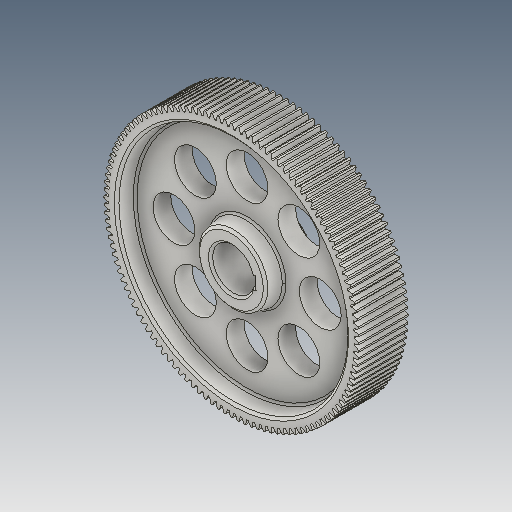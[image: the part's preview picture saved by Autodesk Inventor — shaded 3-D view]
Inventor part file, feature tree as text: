
AUTODESK INVENTOR PART (.ipt)
format: ipt  version: 2025 (Build 290162000, 162)  size: 833,024 bytes
history: native  units: mm (DEFAULTED — no unit token found)
features: other x5, sketch x5, extrude x4, plane x3, mirror x1, fillet x1, chamfer x1
ambient origin geometry x8: Origin, YZ Plane, XZ Plane, XY Plane, X Axis, Y Axis, Z Axis, Center Point
bodies: Solid1 (feature_tree)
feature tree (20):
  other  "{BB8FE430-83BF-418D-8DF9-9B323D3DB9B9}"
  extrude  "Extrusion1"  Depth=47.0mm TaperAngle=0.0deg
  plane  "Work Plane2"
  plane  "Work Plane8"
  plane  "Work Plane9"
  other  "正齿轮"
  extrude  "拉伸2"  Depth=10.0mm TaperAngle=0.0deg
  extrude  "拉伸3"  Depth=0.261799mm TaperAngle=0.0deg
  mirror  "镜像1"
  extrude  "拉伸4"  TaperAngle=0.0deg  [1 undecoded]
  other  "键槽2"
  fillet  "圆角1"  Radius=146.0mm
  chamfer  "倒角1"  [1 undecoded]
  sketch  "Sketch1"  dims[d0=244.0mm d1=47.0mm d2=0.0mm]
  other  "Srf1"
  sketch  "草图3"  dims[d16=146.0mm d17=0.0mm d34=0.261799mm]
  sketch  "草图4"  dims[d39=0.0mm d41=0.0mm d43=146.0mm]
  sketch  "草图5"  dims[d46=146.0mm d47=0.0mm d48=0.0mm d49=40.0mm d50=12.0mm d51=8.0mm d52=10.0mm d53=0.0mm d54=65.0mm d55=220.0mm d56=15.0mm d57=-2.007129mm d58=40.0mm d59=70.0mm d60=80.0mm d62=360.0deg d64=47.0mm d65=0.0mm d66=2.0mm d67=2.0mm d68=2.0mm d69=45.0deg]
  sketch  "草图 - 环形阵列1"  dims[d3=240.0mm d4=10.0mm d5=0.0mm]
  other  "轮毂键槽2"
note: 2 required parameter values undecoded (feature->parameter linkage not recoverable at this tier; creation-order binding heuristic only, values carry confidence <= 0.55)
